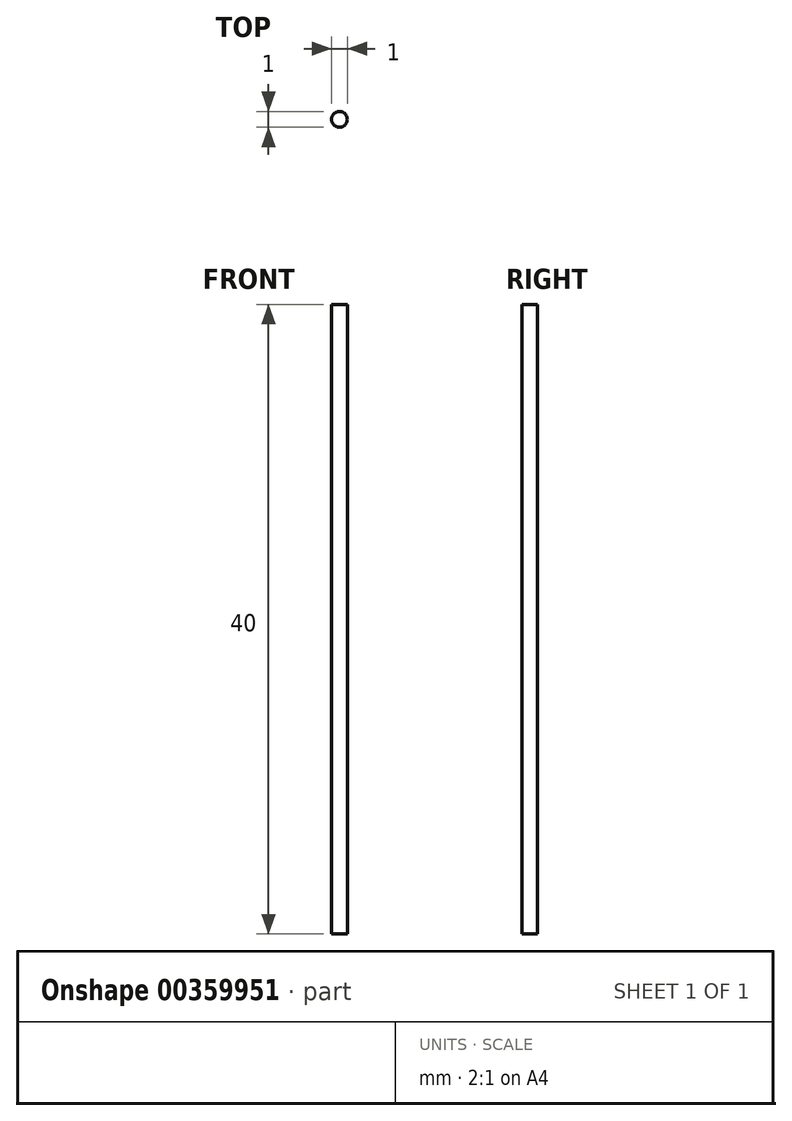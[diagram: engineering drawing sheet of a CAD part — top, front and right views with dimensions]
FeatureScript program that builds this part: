
annotation { "Feature Type Name" : "Feature", "Feature Type Description" : "" }
export const myFeature = defineFeature(function(context is Context, id is Id, definition is map)
    precondition{}
    {
        {
            var Q0;
            Q0=qCreatedBy(makeId("Top.planeOp"),FACE);
            var sketch = newSketch(context, id + "F0", { "sketchPlane" : qUnion([Q0])});
            skCircle(sketch, "E0", {"center": v(0, 0) * mm, "radius": 0.5 * mm});
            skSolve(sketch);
        }
        {
            var Q0;
            Q0 = qSketchRegion(id + "F0", true);
            extrude(context, id + "F1", {"entities" : qUnion([Q0]), "depth" : 40 * mm});
        }
    });
